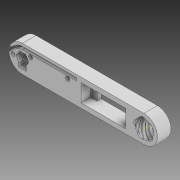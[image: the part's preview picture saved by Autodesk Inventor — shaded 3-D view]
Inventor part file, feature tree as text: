
AUTODESK INVENTOR PART (.ipt)
format: ipt  version: 2020 (Build 240168000, 168)  size: 860,672 bytes
history: native  units: mm
features: sketch x11, extrude x10, plane x2, fillet x2, other x1, helix x1, pattern_circular x1, projected_geometry x1
ambient origin geometry x8: Origin, YZ Plane, XZ Plane, XY Plane, X Axis, Y Axis, Z Axis, Center Point
bodies: Solid1 (feature_tree)
feature tree (29):
  extrude  "Extrusion1"  Depth=10.0mm
  extrude  "Extrusion2"  Depth=10.0mm
  extrude  "Extrusion4"  Depth=2.0mm
  extrude  "Extrusion5"  Depth=40.0mm
  plane  "Work Plane1"
  extrude  "Extrusion6"  Depth=13.0mm
  extrude  "Extrusion7"  Depth=15.0mm
  sketch  "Sketch8"  dims[d21=4.7mm]
  other  "Work Axis1"
  helix  "Coil1"  [1 undecoded]
  fillet  "Fillet1"  [1 undecoded]
  pattern_circular  "Circular Pattern1"  [2 undecoded]
  extrude  "Extrusion8"  Depth=10.0mm TaperAngle=0.0deg
  fillet  "Fillet2"  Radius=12.6mm
  extrude  "Extrusion9"  TaperAngle=0.0deg  [1 undecoded]
  plane  "Work Plane2"
  extrude  "Extrusion10"  Depth=10.0mm
  extrude  "Extrusion11"  Depth=10.0mm
  sketch  "Sketch1"  dims[d0=90.0mm d1=10.0mm]
  sketch  "Sketch2"  dims[d2=10.0mm d3=0.0mm d4=5.5mm]
  sketch  "Sketch4"  dims[d5=0.0mm d6=0.0mm d10=2.0mm]
  sketch  "Sketch5"  dims[d11=2.0mm d12=40.0mm]
  sketch  "Sketch6"  dims[d13=4.0mm d14=0.0mm d15=13.0mm]
  sketch  "Sketch7"  dims[d16=33.0mm d17=15.0mm d18=11.75mm d19=0.0mm d20=-2.0mm]
  sketch  "Sketch9"  dims[d22=4.7mm]
  sketch  "Sketch11"  dims[d23=2.5mm]
  sketch  "Sketch12"  dims[d24=2.5mm]
  sketch  "Sketch13"  dims[d25=3.0mm d26=3.0mm d27=2.0mm d28=0.0mm d29=12.6mm d30=0.0mm d31=0.0mm d34=25.0mm d35=10.0mm d36=10.0mm d37=0.0mm d38=90.0deg d39=90.0deg d40=0.0mm d41=0.0mm d43=1.5mm d44=0.75mm d45=0.5mm d46=50.0mm d47=360.0deg d49=8.0mm d50=3.0mm d51=2.0mm d52=2.0mm d53=3.0mm d56=7.0mm d57=0.0mm d58=0.5mm d59=6.0mm d60=3.3mm d61=10.0mm d62=0.0mm d63=-3.5mm d64=5.8mm d65=2.6mm d66=0.0mm d67=8.1mm d68=3.0mm d69=0.0mm d70=4.0mm d71=6.0mm d72=1.0mm d73=0.0mm d74=10.0mm]
  projected_geometry  "Projected Loop1"
note: 5 required parameter values undecoded (feature->parameter linkage not recoverable at this tier; creation-order binding heuristic only, values carry confidence <= 0.55)
